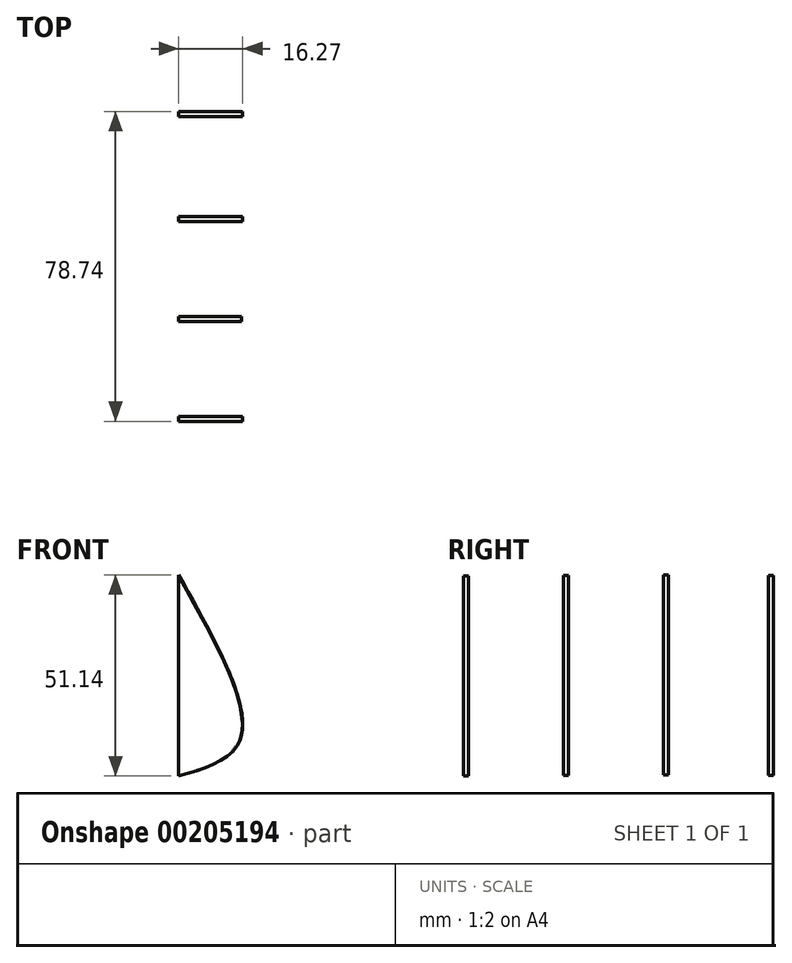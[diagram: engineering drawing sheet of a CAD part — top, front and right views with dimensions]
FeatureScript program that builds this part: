
annotation { "Feature Type Name" : "Feature", "Feature Type Description" : "" }
export const myFeature = defineFeature(function(context is Context, id is Id, definition is map)
    precondition{}
    {
        {
            var Q0;
            Q0=qCreatedBy(makeId("Front.planeOp"),FACE);
            var sketch = newSketch(context, id + "F0", { "sketchPlane" : qUnion([Q0])});
            skLineSegment(sketch, "E0", {"start": v(0, -22.25) * mm, "end": v(0, 28.55) * mm});
            skFitSpline(sketch, "E1", {"points": [v(0, -22.25) * mm, v(15.7, -13.13) * mm, v(0, 28.55) * mm], "startDerivative": vector(53.17, 14.66) * mm, "endDerivative": vector(-45.9, 81.99) * mm});
            skSolve(sketch);
        }
        {
            var Q0;
            Q0=qCreatedBy(makeId("Front.planeOp"),FACE);
            cPlane(context, id + "F1", {"entities" : qUnion([Q0]), "cplaneType" : CPlaneType.OFFSET, "offset" : 25.4 * mm, "width" : 152.4 * mm, "height" : 152.4 * mm});
        }
        {
            var Q0;
            Q0=qCreatedBy(id+"F1.planeOp",FACE);
            var sketch = newSketch(context, id + "F2", { "sketchPlane" : qUnion([Q0])});
            skLineSegment(sketch, "E2", {"start": v(0, -22.35) * mm, "end": v(0, 28.45) * mm});
            skFitSpline(sketch, "E3", {"points": [v(0, -22.35) * mm, v(15.46, -13.13) * mm, v(0, 28.45) * mm], "startDerivative": vector(52.4, 15.05) * mm, "endDerivative": vector(-45.18, 81.63) * mm});
            skSolve(sketch);
        }
        {
            var Q0;
            Q0=qCreatedBy(makeId("Front.planeOp"),FACE);
            cPlane(context, id + "F3", {"entities" : qUnion([Q0]), "cplaneType" : CPlaneType.OFFSET, "offset" : 25.4 * mm, "oppositeDirection" : true, "width" : 152.4 * mm, "height" : 152.4 * mm});
        }
        {
            var Q0;
            Q0=qCreatedBy(id+"F3.planeOp",FACE);
            var sketch = newSketch(context, id + "F4", { "sketchPlane" : qUnion([Q0])});
            skLineSegment(sketch, "E4", {"start": v(0, -22.35) * mm, "end": v(0, 28.45) * mm});
            skFitSpline(sketch, "E5", {"points": [v(0, -22.35) * mm, v(15.7, -12.89) * mm, v(0, 28.45) * mm], "startDerivative": vector(53.01, 15.58) * mm, "endDerivative": vector(-45.87, 81.28) * mm});
            skSolve(sketch);
        }
        {
            var Q0;
            Q0=qCreatedBy(id+"F1.planeOp",FACE);
            cPlane(context, id + "F5", {"entities" : qUnion([Q0]), "cplaneType" : CPlaneType.OFFSET, "offset" : 25.4 * mm, "width" : 152.4 * mm, "height" : 152.4 * mm});
        }
        {
            var Q0;
            Q0=qCreatedBy(id+"F5.planeOp",FACE);
            var sketch = newSketch(context, id + "F6", { "sketchPlane" : qUnion([Q0])});
            skLineSegment(sketch, "E6", {"start": v(0, -22.6) * mm, "end": v(0, 28.2) * mm});
            skFitSpline(sketch, "E7", {"points": [v(0, -22.6) * mm, v(15.7, -13.13) * mm, v(0, 28.2) * mm], "startDerivative": vector(53.01, 15.57) * mm, "endDerivative": vector(-45.87, 81.28) * mm});
            skSolve(sketch);
        }
        {
            var Q0;
            Q0=makeQuery(id+"F6.imprint","IMPRINT",FACE,{"disambiguationData":[TD([[makeQuery(id+"F6.imprint","IMPRINT",EDGE,{"derivedFrom":sQuery(id+"F6.wireOp",EDGE,"E6")}),-1.0]])]});
            extrude(context, id + "F7", {"entities" : qUnion([Q0]), "depth" : 1.27 * mm});
        }
        {
            var Q0;
            Q0=makeQuery(id+"F4.imprint","IMPRINT",FACE,{"disambiguationData":[TD([[makeQuery(id+"F4.imprint","IMPRINT",EDGE,{"derivedFrom":sQuery(id+"F4.wireOp",EDGE,"E4")}),-1.0]])]});
            extrude(context, id + "F8", {"entities" : qUnion([Q0]), "oppositeDirection" : true, "depth" : 1.27 * mm});
        }
        {
            var Q0;
            Q0=makeQuery(id+"F0.imprint","IMPRINT",FACE,{"disambiguationData":[TD([[makeQuery(id+"F0.imprint","IMPRINT",EDGE,{"derivedFrom":sQuery(id+"F0.wireOp",EDGE,"E0")}),-1.0]])]});
            extrude(context, id + "F9", {"entities" : qUnion([Q0]), "depth" : 1.27 * mm});
        }
        {
            var Q0;
            Q0=makeQuery(id+"F2.imprint","IMPRINT",FACE,{"disambiguationData":[TD([[makeQuery(id+"F2.imprint","IMPRINT",EDGE,{"derivedFrom":sQuery(id+"F2.wireOp",EDGE,"E2")}),-1.0]])]});
            extrude(context, id + "F10", {"entities" : qUnion([Q0]), "depth" : 1.27 * mm});
        }
    });
